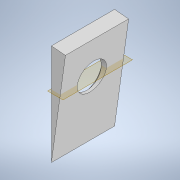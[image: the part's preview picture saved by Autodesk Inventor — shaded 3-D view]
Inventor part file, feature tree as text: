
AUTODESK INVENTOR PART (.ipt)
format: ipt  version: 2021.1 (Build 251245000, 245)  size: 365,056 bytes
history: native  units: in
note: dims shown in document units (in); Inventor stores cm internally (conversion verified against a paired STEP export)
features: extrude x6, sketch x6, plane x1, split x1
ambient origin geometry x8: Origin, YZ Plane, XZ Plane, XY Plane, X Axis, Y Axis, Z Axis, Center Point
bodies: Solid1 (feature_tree)
feature tree (14):
  extrude  "MainStructure"  Depth=0.5622in
  extrude  "PipeHole"  TaperAngle=0.0deg  [1 undecoded]
  extrude  "AngleForTopRelief"  TaperAngle=0.0deg  [1 undecoded]
  extrude  "TextForBack"  TaperAngle=0.0deg  [1 undecoded]
  extrude  "ReliefForHole"  Depth=0.04in TaperAngle=0.0deg
  extrude  "TextForSmallText"  [1 undecoded]
  plane  "Work Plane2"
  split  "Split7"
  sketch  "Sketch1"  dims[d1=0.055in d2=0.5622in]
  sketch  "Sketch2"  dims[d4=0.0in d7=0.0in d8=0.0in]
  sketch  "Sketch6"  dims[d19=0.0in d20=0.0in d25=0.0in]
  sketch  "Sketch7"  dims[d28=0.0in d29=0.0in]
  sketch  "Sketch8"  dims[d35=0.375in d36=0.04in d37=0.0in]
  sketch  "Sketch9"  dims[d42=2.5in]
note: 4 required parameter values undecoded (feature->parameter linkage not recoverable at this tier; creation-order binding heuristic only, values carry confidence <= 0.55)
